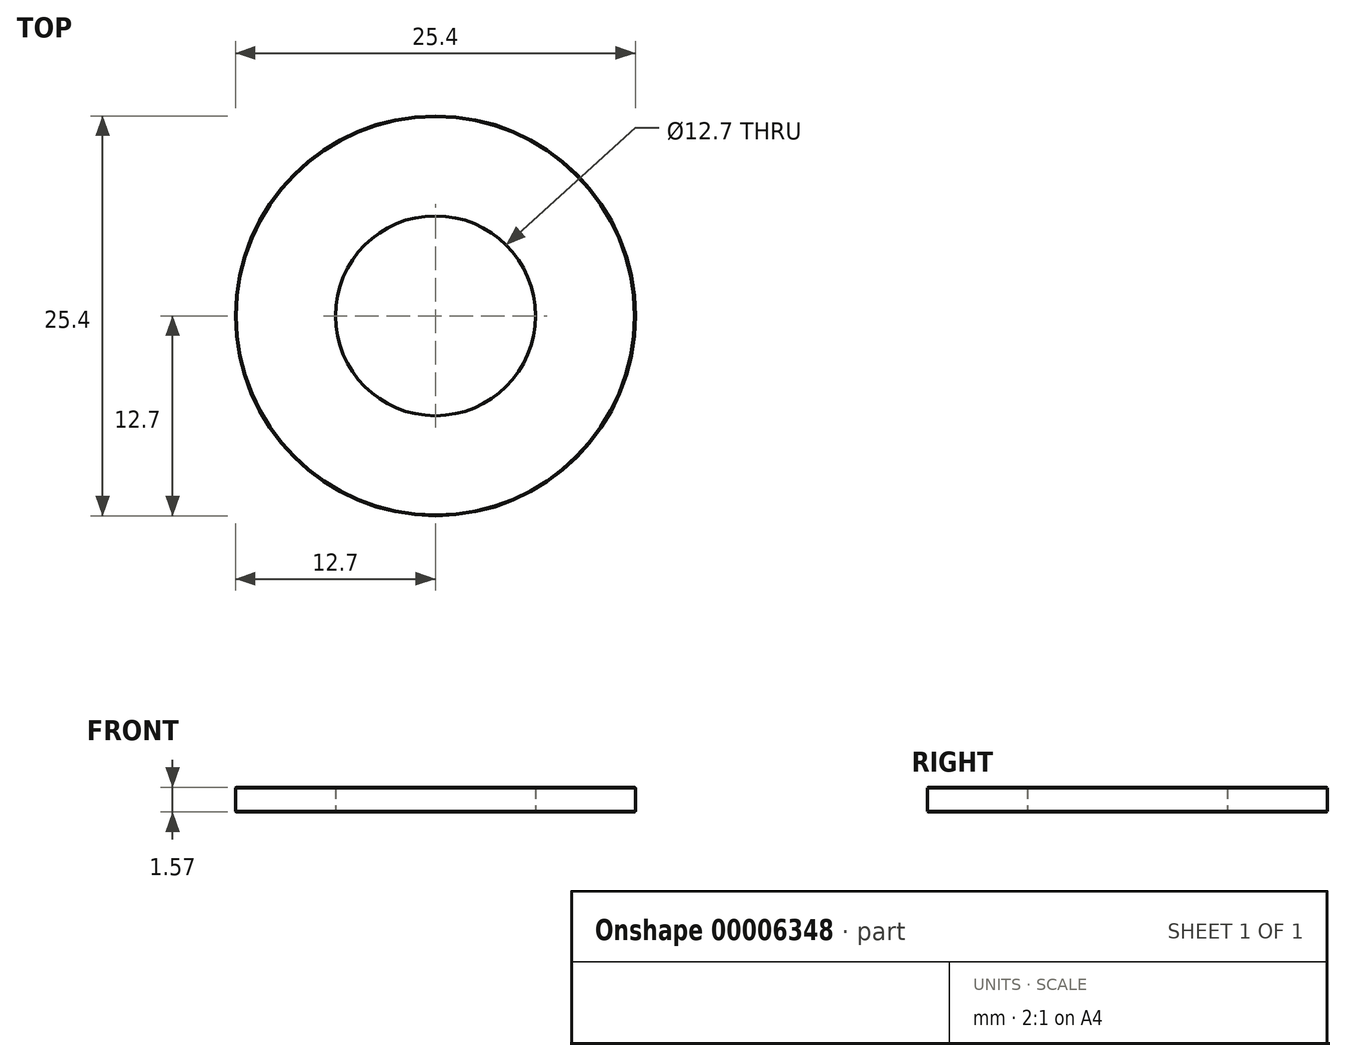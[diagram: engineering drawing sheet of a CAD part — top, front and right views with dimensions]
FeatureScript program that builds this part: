
annotation { "Feature Type Name" : "Feature", "Feature Type Description" : "" }
export const myFeature = defineFeature(function(context is Context, id is Id, definition is map)
    precondition{}
    {
        {
            var Q0;
            Q0=qCreatedBy(makeId("Top.planeOp"),FACE);
            var sketch = newSketch(context, id + "F0", { "sketchPlane" : qUnion([Q0])});
            skCircle(sketch, "E0", {"center": v(0, 0) * mm, "radius": 6.35 * mm});
            skCircle(sketch, "E1", {"center": v(0, 0) * mm, "radius": 12.7 * mm});
            skSolve(sketch);
        }
        {
            var Q0;
            Q0 = qSketchRegion(id + "F0", true);
            extrude(context, id + "F1", {"entities" : qUnion([Q0]), "depth" : 1.57 * mm});
        }
        {
            var Q0;
            Q0=makeQuery(id+"F1.opExtrude","CAP_EDGE",EDGE,{"disambiguationData":[OSD([sQuery(id+"F0.wireOp",EDGE,"E1")])],"isStart":false});
            var Q1;
            Q1=makeQuery(id+"F1.opExtrude","CAP_EDGE",EDGE,{"disambiguationData":[OSD([sQuery(id+"F0.wireOp",EDGE,"E1")])],"isStart":true});
            chamfer(context, id + "F2", {"entities" : qUnion([Q0, Q1]), "width" : 0.05 * mm, "tangentPropagation" : true});
        }
    });
